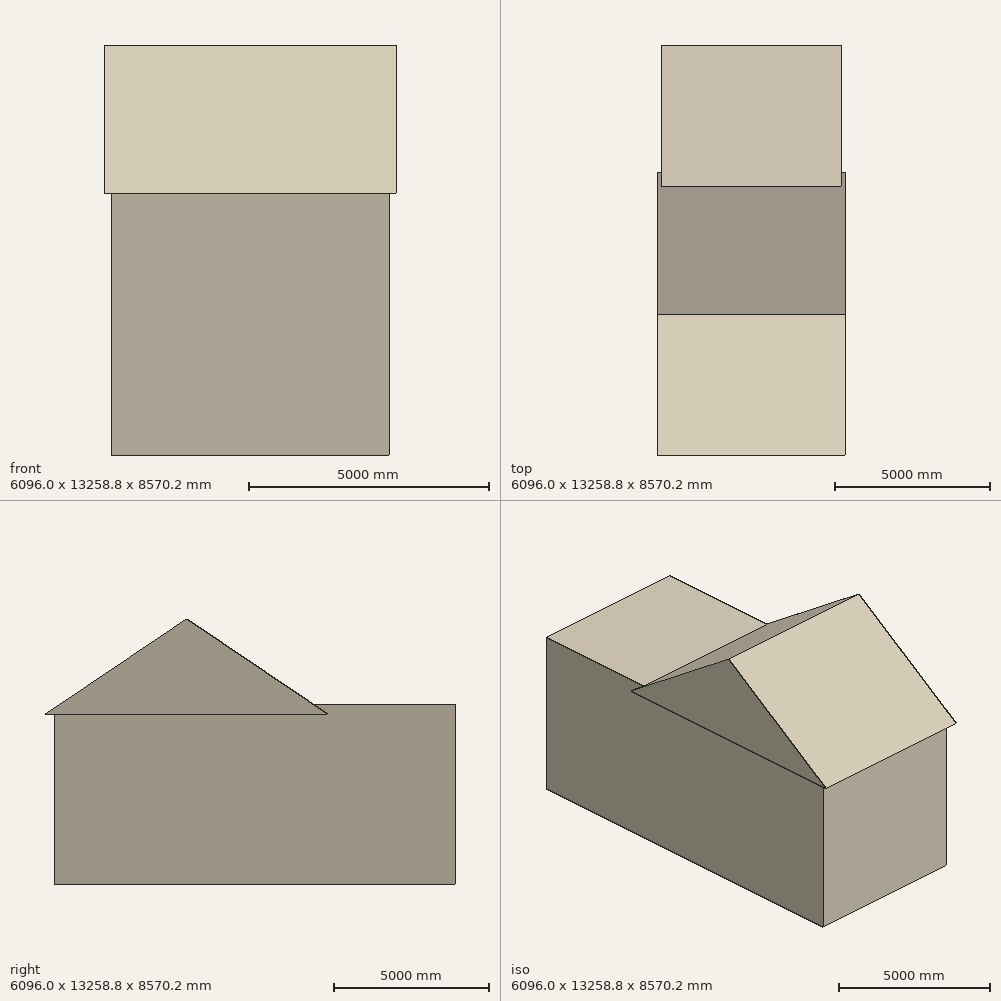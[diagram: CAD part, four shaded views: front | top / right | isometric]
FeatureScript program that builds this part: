
annotation { "Feature Type Name" : "Feature", "Feature Type Description" : "" }
export const myFeature = defineFeature(function(context is Context, id is Id, definition is map)
    precondition{}
    {
        {
            var Q0;
            Q0=qCreatedBy(makeId("Right.planeOp"),FACE);
            var sketch = newSketch(context, id + "F0", { "sketchPlane" : qUnion([Q0])});
            skLineSegment(sketch, "E0", {"start": v(-4572, -3083.85) * mm, "end": v(0, 0) * mm});
            skLineSegment(sketch, "E1", {"start": v(0, 0) * mm, "end": v(4572, -3083.85) * mm});
            skLineSegment(sketch, "E2", {"start": v(4572, -3083.85) * mm, "end": v(-4572, -3083.85) * mm});
            skLineSegment(sketch, "E3", {"start": v(-4572, -3083.85) * mm, "end": v(-4267.2, -3083.85) * mm});
            skLineSegment(sketch, "E4.top", {"start": v(-4267.2, -8570.25) * mm, "end": v(8686.8, -8570.25) * mm});
            skLineSegment(sketch, "E4.right", {"start": v(8686.8, -2779.05) * mm, "end": v(8686.8, -8570.25) * mm});
            skLineSegment(sketch, "E5", {"start": v(4120.12, -2779.05) * mm, "end": v(8686.8, -2779.05) * mm});
            skLineSegment(sketch, "E6", {"start": v(-4267.2, -3083.85) * mm, "end": v(-4267.2, -8570.25) * mm});
            skSolve(sketch);
        }
        {
            var Q0;
            {var subQ3=sQuery(id+"F0.wireOp",EDGE,"E0");Q0=makeQuery(id+"F0.imprint","IMPRINT",FACE,{"disambiguationData":[TD([[makeQuery(id+"F0.imprint","IMPRINT",EDGE,{"derivedFrom":subQ3}),-1.0]])]});}
            extrude(context, id + "F1", {"entities" : qUnion([Q0]), "endBound" : BoundingType.SYMMETRIC, "depth" : 6096 * mm});
        }
        {
            var Q0;
            {var subQ0=sQuery(id+"F0.wireOp",EDGE,"E2");Q0=makeQuery(id+"F0.imprint","IMPRINT",FACE,{"disambiguationData":[TD([[makeQuery(id+"F0.imprint","IMPRINT",EDGE,{"derivedFrom":subQ0}),1.0]])]});}
            extrude(context, id + "F2", {"entities" : qUnion([Q0]), "operationType" : NewBodyOperationType.ADD, "endBound" : BoundingType.SYMMETRIC, "depth" : 5791.2 * mm});
        }
    });
